FCSTD DOCUMENT  (FreeCAD 1.0R39109 (Git))
Label: barrel
License: All rights reserved
LicenseURL: https://en.wikipedia.org/wiki/All_rights_reserved
objects: App::Link×10, App::FeaturePython×9, Assembly::JointGroup×1, Assembly::AssemblyObject×1
EXTERNAL_REF file=barrelMount.FCStd obj=Body
EXTERNAL_REF file=barrelSpacer.FCStd obj=Body
EXTERNAL_REF file=barrelSideOpen.FCStd obj=Body
EXTERNAL_REF file=../roundFlap.FCStd obj=Body

FEATURE [App::Link] Body
  LinkedObject = -> <external barrelMount.FCStd>#Body
FEATURE [App::FeaturePython] GroundedJoint  # Assembly grounded joint (typed FeaturePython)
  ObjectToGround = -> Body
FEATURE [App::Link] Body001  label="Spacer1"
  LinkPlacement = pos=(58,31.8049,3.72e-14) rot=(0.57735,0.57735,-0.57735;4.18879rad)
  LinkedObject = -> <external barrelSpacer.FCStd>#Body
  Placement = pos=(58,31.8049,3.72e-14) rot=(0.57735,0.57735,-0.57735;4.18879rad)
FEATURE [App::Link] Body002  label="Spacer2"
  LinkPlacement = pos=(58,-1.99704,-31.7421) rot=(0.57735,0.57735,-0.57735;4.18879rad)
  LinkedObject = -> <external barrelSpacer.FCStd>#Body
  Placement = pos=(58,-1.99704,-31.7421) rot=(0.57735,0.57735,-0.57735;4.18879rad)
FEATURE [App::Link] Body003  label="Spacer3"
  LinkPlacement = pos=(3,-31.8049,1.15e-14) rot=(0.57735,0.57735,0.57735;2.0944rad)
  LinkedObject = -> <external barrelSpacer.FCStd>#Body
  Placement = pos=(3,-31.8049,1.15e-14) rot=(0.57735,0.57735,0.57735;2.0944rad)
FEATURE [App::Link] Body004  label="Spacer4"
  LinkPlacement = pos=(3,1.99704,31.7421) rot=(0.57735,0.57735,0.57735;2.0944rad)
  LinkedObject = -> <external barrelSpacer.FCStd>#Body
  Placement = pos=(3,1.99704,31.7421) rot=(0.57735,0.57735,0.57735;2.0944rad)
FEATURE [App::Link] Body007  label="SideOpen"
  LinkPlacement = pos=(61,3.75e-14,5.47e-14) rot=(0,1,0;3.14159rad)
  LinkedObject = -> <external barrelSideOpen.FCStd>#Body
  Placement = pos=(61,3.75e-14,5.47e-14) rot=(0,1,0;3.14159rad)
FEATURE [App::Link] Body008  label="Flap2"
  LinkPlacement = pos=(30.5,-35.345,41.8018) rot=(1,0,0;4.64956rad)
  LinkedObject = -> <external ../roundFlap.FCStd>#Body
  Placement = pos=(30.5,-35.345,41.8018) rot=(1,0,0;4.64956rad)
FEATURE [App::Link] Body009  label="Flap1"
  LinkPlacement = pos=(30.3278,-36.327,-41.8389) rot=(0,0.693562,0.720397;3.14159rad)
  LinkedObject = -> <external ../roundFlap.FCStd>#Body
  Placement = pos=(30.3278,-36.327,-41.8389) rot=(0,0.693562,0.720397;3.14159rad)
FEATURE [App::Link] Body010  label="Unnamed"
FEATURE [App::Link] Body011  label="Unnamed"
FEATURE [App::FeaturePython] Joint  label="Fixed"  # Assembly joint (typed FeaturePython)
  Activated = true
  AngleMax = 0
  AngleMin = 0
  Detach1 = false
  Detach2 = false
  Distance = 0
  Distance2 = 0
  EnableAngleMax = false
  EnableAngleMin = false
  EnableLengthMax = false
  EnableLengthMin = false
  JointType = 0 (Fixed)
  LengthMax = 0
  LengthMin = 0
  Placement2 = pos=(3,-31.8049,1.15e-14) rot=(0.57735,0.57735,0.57735;2.0944rad)
  Reference1 = -> Assembly [Body003.Pad.Edge5,Body003.Pad.Edge5]
  Reference2 = -> Assembly [Body.Chamfer001.Edge234,Body.Chamfer001.Edge234]
FEATURE [App::FeaturePython] Joint008  label="Fixed001"  # Assembly joint (typed FeaturePython)
  Activated = true
  AngleMax = 0
  AngleMin = 0
  Detach1 = false
  Detach2 = false
  Distance = 0
  Distance2 = 0
  EnableAngleMax = false
  EnableAngleMin = false
  EnableLengthMax = false
  EnableLengthMin = false
  JointType = 0 (Fixed)
  LengthMax = 0
  LengthMin = 0
  Placement1 = pos=(0,0,55) rot=(0,0,1;0rad)
  Placement2 = pos=(3,31.8049,-1.78e-14) rot=(0.57735,0.57735,0.57735;2.0944rad)
  Reference1 = -> Assembly [Body001.Pad.Edge6,Body001.Pad.Edge6]
  Reference2 = -> Assembly [Body.Chamfer001.Edge190,Body.Chamfer001.Edge190]
FEATURE [App::FeaturePython] Joint009  label="Fixed002"  # Assembly joint (typed FeaturePython)
  Activated = true
  AngleMax = 0
  AngleMin = 0
  Detach1 = false
  Detach2 = false
  Distance = 0
  Distance2 = 0
  EnableAngleMax = false
  EnableAngleMin = false
  EnableLengthMax = false
  EnableLengthMin = false
  JointType = 0 (Fixed)
  LengthMax = 0
  LengthMin = 0
  Placement2 = pos=(3,1.99704,31.7421) rot=(0.57735,0.57735,0.57735;2.0944rad)
  Reference1 = -> Assembly [Body004.Pad.Edge5,Body004.Pad.Edge5]
  Reference2 = -> Assembly [Body.Chamfer001.Edge184,Body.Chamfer001.Edge184]
FEATURE [App::FeaturePython] Joint010  label="Fixed003"  # Assembly joint (typed FeaturePython)
  Activated = true
  AngleMax = 0
  AngleMin = 0
  Detach1 = false
  Detach2 = false
  Distance = 0
  Distance2 = 0
  EnableAngleMax = false
  EnableAngleMin = false
  EnableLengthMax = false
  EnableLengthMin = false
  JointType = 0 (Fixed)
  LengthMax = 0
  LengthMin = 0
  Placement1 = pos=(0,0,55) rot=(0,0,1;0rad)
  Placement2 = pos=(3,-1.99704,-31.7421) rot=(0.57735,0.57735,0.57735;2.0944rad)
  Reference1 = -> Assembly [Body002.Pad.Edge6,Body002.Pad.Edge6]
  Reference2 = -> Assembly [Body.Chamfer001.Edge240,Body.Chamfer001.Edge240]
FEATURE [App::FeaturePython] Joint011  label="Fixed004"  # Assembly joint (typed FeaturePython)
  Activated = true
  AngleMax = 0
  AngleMin = 0
  Detach1 = false
  Detach2 = false
  Distance = 0
  Distance2 = 0
  EnableAngleMax = false
  EnableAngleMin = false
  EnableLengthMax = false
  EnableLengthMin = false
  JointType = 0 (Fixed)
  LengthMax = 0
  LengthMin = 0
  Placement1 = pos=(3,-31.8049,6e-16) rot=(0.57735,0.57735,0.57735;2.0944rad)
  Placement2 = pos=(0,0,55) rot=(0,0,1;0rad)
  Reference1 = -> Assembly [Body007.Pocket001.Edge107,Body007.Pocket001.Edge107]
  Reference2 = -> Assembly [Body003.Pad.Edge6,Body003.Pad.Edge6]
FEATURE [App::FeaturePython] Joint012  label="Fixed005"  # Assembly joint (typed FeaturePython)
  Activated = true
  AngleMax = 0
  AngleMin = 0
  Detach1 = false
  Detach2 = false
  Distance = 0
  Distance2 = 0
  EnableAngleMax = false
  EnableAngleMin = false
  EnableLengthMax = false
  EnableLengthMin = false
  JointType = 0 (Fixed)
  LengthMax = 0
  LengthMin = 0
  Placement1 = pos=(3,31.8049,-2e-16) rot=(0.57735,0.57735,0.57735;2.0944rad)
  Reference1 = -> Assembly [Body007.Pocket001.Edge75,Body007.Pocket001.Edge75]
  Reference2 = -> Assembly [Body001.Pad.Edge5,Body001.Pad.Edge5]
FEATURE [App::FeaturePython] Joint013  label="Cylindrical"  # Assembly joint (typed FeaturePython)
  Activated = true
  AngleMax = 0
  AngleMin = 0
  Detach1 = false
  Detach2 = false
  Distance = 0
  Distance2 = 0
  EnableAngleMax = false
  EnableAngleMin = false
  EnableLengthMax = false
  EnableLengthMin = false
  JointType = 2 (Cylindrical)
  LengthMax = 0
  LengthMin = 0
  Placement1 = pos=(29,39.5,0.5) rot=(0.576441,-0.576441,-0.576441;2.0944rad)
  Placement2 = pos=(1.5,-37.3262,-2.34837) rot=(0.706932,-0.022216,0.706932;3.18602rad)
  Reference1 = -> Assembly [Body009.Face8,Body009.Face8]
  Reference2 = -> Assembly [Body.Face66,Body.Face66]
FEATURE [App::FeaturePython] Joint014  label="Cylindrical001"  # Assembly joint (typed FeaturePython)
  Activated = true
  AngleMax = 0
  AngleMin = 0
  Detach1 = false
  Detach2 = false
  Distance = 0
  Distance2 = 0
  EnableAngleMax = false
  EnableAngleMin = false
  EnableLengthMax = false
  EnableLengthMin = false
  JointType = 2 (Cylindrical)
  LengthMax = 0
  LengthMin = 0
  Placement1 = pos=(-29,39.5,0.5) rot=(-0.57735,0.57735,0.57735;4.18879rad)
  Placement2 = pos=(1.5,-37.3262,2.34837) rot=(0.706932,0.022216,0.706932;3.09717rad)
  Reference1 = -> Assembly [Body008.Face2,Body008.Face2]
  Reference2 = -> Assembly [Body.Face60,Body.Face60]
FEATURE [Assembly::JointGroup] Joints
  Group = -> [GroundedJoint,Joint,Joint008,Joint009,Joint010,Joint011,Joint012,Joint013,Joint014]
FEATURE [Assembly::AssemblyObject] Assembly
  Group = -> [Joints,Body,GroundedJoint,Body001,Body002,Body003,Body004,Body007,Body008,Body009,Joint,Joint008,Joint009,Joint010,Joint011,Joint012,Joint013,Joint014]
  Origin = -> Origin
  Type = Assembly

RESOLVED EXTERNAL PARTS (link-assembly join: the EXTERNAL_REF files above that resolve inside this repo's crawl, each included once):
---- part ../roundFlap.FCStd = doc fcstd_2553a03e6fe1 ----
FCSTD DOCUMENT  (FreeCAD 1.0R39109 (Git))
Label: roundFlap
License: All rights reserved
LicenseURL: https://en.wikipedia.org/wiki/All_rights_reserved
objects: Sketcher::SketchObject×2, PartDesign::Pad×2, PartDesign::Mirrored×1, PartDesign::Body×1
note: 13 computed .brp shape members not serialized (recipe doc carries the construction recipe); baked Part::Feature solids carry a one-line shape summary decoded from their .brp

FEATURE [Sketcher::SketchObject] Sketch
  ArcFitTolerance = 1e-06
  AttachmentSupport = -> [XY_Plane]
  FullyConstrained = true
  MakeInternals = false
  MapMode = 5
  sketch-geometry (5):
    g0: LineSegment StartX=-27 StartY=0 StartZ=0 EndX=0 EndY=0 EndZ=0
    g1: LineSegment StartX=0 StartY=0 StartZ=0 EndX=0 EndY=40 EndZ=0
    g2: LineSegment StartX=0 StartY=40 StartZ=0 EndX=-27 EndY=40 EndZ=0
    g3: LineSegment StartX=-27 StartY=40 StartZ=0 EndX=-27 EndY=0 EndZ=0
    g4: GeomPoint [constr] X=0 Y=0 Z=0
  constraints (12):
    c: Coincident(g0,g1)
    c: Coincident(g1,g2)
    c: Coincident(g2,g3)
    c: Coincident(g3,g0)
    c: Horizontal(g0)
    c: Horizontal(g2)
    c: Vertical(g1)
    c: Vertical(g3)
    c: Coincident(g4,g-1)
    c: Distance(g0,g2) = 40
    c: Coincident(g0,g4)
    c: DistanceX(g0,g0) = 27
FEATURE [PartDesign::Pad] Pad
  Direction = (0,0,1)
  Length = 1
  Length2 = 10
  Profile = -> Sketch
  ReferenceAxis = -> Sketch [N_Axis]
  Refine = true
  Suppressed = false
  Type = 0
FEATURE [Sketcher::SketchObject] Sketch001
  ArcFitTolerance = 1e-06
  AttachmentSupport = -> [Pad]
  FullyConstrained = true
  MakeInternals = false
  MapMode = 5
  Placement = pos=(-27,0,0) rot=(0.57735,-0.57735,-0.57735;2.0944rad)
  sketch-geometry (1):
    g0: Circle CenterX=-39.5 CenterY=0.5 CenterZ=0 NormalX=0 NormalY=0 NormalZ=1 AngleXU=0 Radius=0.5
  constraints (3):
    c: Tangent(g0,g-1)
    c: Diameter(g0) = 1
    c: DistanceX(g0,g-1) = 39.5
FEATURE [PartDesign::Pad] Pad001
  BaseFeature = -> Pad
  Direction = (-1,0,0)
  Length = 4
  Length2 = 10
  Profile = -> Sketch001
  ReferenceAxis = -> Sketch001 [N_Axis]
  Refine = true
  Suppressed = false
  Type = 0
FEATURE [PartDesign::Mirrored] Mirrored
  BaseFeature = -> Pad001
  MirrorPlane = -> YZ_Plane
  Refine = true
  Suppressed = false
  TransformMode = 1
FEATURE [PartDesign::Body] Body
  AllowCompound = false
  Group = -> [Sketch,Pad,Sketch001,Pad001,Mirrored]
  Origin = -> Origin
  Tip = -> Mirrored
---- part barrelMount.FCStd = doc fcstd_386b91f5edca ----
FCSTD DOCUMENT  (FreeCAD 1.0R39109 (Git))
Label: barrelMount
License: All rights reserved
LicenseURL: https://en.wikipedia.org/wiki/All_rights_reserved
objects: Sketcher::SketchObject×5, PartDesign::Pocket×3, PartDesign::Pad×2, PartDesign::Fillet×2, PartDesign::Chamfer×2, PartDesign::PolarPattern×1, PartDesign::Body×1
note: 40 computed .brp shape members not serialized (recipe doc carries the construction recipe); baked Part::Feature solids carry a one-line shape summary decoded from their .brp

FEATURE [Sketcher::SketchObject] Sketch
  ArcFitTolerance = 1e-06
  AttachmentSupport = -> [YZ_Plane]
  FullyConstrained = false
  MakeInternals = false
  MapMode = 5
  Placement = pos=(0,0,0) rot=(0.57735,0.57735,0.57735;2.0944rad)
  sketch-geometry (2):
    g0: Circle CenterX=0 CenterY=0 CenterZ=0 NormalX=0 NormalY=0 NormalZ=1 AngleXU=0 Radius=40
    g1: GeomPoint [constr] X=0 Y=0 Z=0
  constraints (1):
    c: Diameter(g0) = 80
FEATURE [PartDesign::Pad] Pad
  Direction = (1,0,0)
  Length = 3
  Length2 = 10
  Placement = pos=(0,0,0) rot=(1,1,1;2.0944rad)
  Profile = -> Sketch
  ReferenceAxis = -> Sketch [N_Axis]
  Refine = true
  Suppressed = false
  Type = 0
FEATURE [Sketcher::SketchObject] Sketch001
  ArcFitTolerance = 1e-06
  AttachmentSupport = -> [Pad]
  ExternalGeometry = -> [Pad]
  FullyConstrained = true
  MakeInternals = false
  MapMode = 5
  Placement = pos=(3,0,0) rot=(0.57735,0.57735,0.57735;2.0944rad)
  sketch-geometry (1):
    g0: Circle CenterX=0 CenterY=37.4 CenterZ=0 NormalX=0 NormalY=0 NormalZ=1 AngleXU=0 Radius=1.6
  constraints (3):
    c: PointOnObject(g0,g-2)
    c: Diameter(g0) = 3.2
    c: Distance(g0,g-3) = 1
FEATURE [PartDesign::Pocket] Pocket
  BaseFeature = -> Pad
  Direction = (-1,0,0)
  Length = 5
  Length2 = 5
  Placement = pos=(0,0,0) rot=(1,1,1;2.0944rad)
  Profile = -> Sketch001
  ReferenceAxis = -> Sketch001 [N_Axis]
  Refine = true
  Suppressed = false
  Type = 1
FEATURE [PartDesign::PolarPattern] PolarPattern
  Angle = 360
  Axis = -> Sketch001 [N_Axis]
  BaseFeature = -> Pocket
  Mode = 0
  Occurrences = 50
  Offset = 120
  Originals = -> [Pocket]
  Placement = pos=(0,0,0) rot=(1,1,1;2.0944rad)
  Refine = true
  Suppressed = false
  TransformMode = 0
FEATURE [Sketcher::SketchObject] Sketch002
  ArcFitTolerance = 1e-06
  AttachmentSupport = -> [PolarPattern]
  ExternalGeometry = -> [PolarPattern]
  FullyConstrained = true
  MakeInternals = false
  MapMode = 5
  Placement = pos=(3,0,0) rot=(0.57735,0.57735,0.57735;2.0944rad)
  sketch-geometry (27):
    g0: Circle [constr] CenterX=0 CenterY=0 CenterZ=0 NormalX=0 NormalY=0 NormalZ=1 AngleXU=0 Radius=31.5
    g1: Circle CenterX=1.99704 CenterY=31.7421 CenterZ=0 NormalX=0 NormalY=0 NormalZ=1 AngleXU=0 Radius=1.6
    g2: Circle CenterX=31.8049 CenterY=1.18e-14 CenterZ=0 NormalX=0 NormalY=0 NormalZ=1 AngleXU=0 Radius=1.6
    g3: Circle CenterX=-1.99704 CenterY=-31.7421 CenterZ=0 NormalX=0 NormalY=0 NormalZ=1 AngleXU=0 Radius=1.6
    g4: Circle CenterX=-31.8049 CenterY=-8.4e-15 CenterZ=0 NormalX=0 NormalY=0 NormalZ=1 AngleXU=0 Radius=1.6
    g5: ArcOfCircle CenterX=1.99704 CenterY=31.7421 CenterZ=0 NormalX=0 NormalY=0 NormalZ=1 AngleXU=0 Radius=4.6 StartAngle=4.82195 EndAngle=6.08164
    g6: LineSegment StartX=-2.5 StartY=31.4006 StartZ=0 EndX=-2.5 EndY=2.5 EndZ=0
    g7: LineSegment StartX=2.5 StartY=2.5 StartZ=0 EndX=2.5 EndY=27.1697 EndZ=0
    g8: LineSegment StartX=2.5 StartY=-2.5 StartZ=0 EndX=2.5 EndY=-31.4006 EndZ=0
    g9: LineSegment StartX=-2.5 StartY=-27.1697 StartZ=0 EndX=-2.5 EndY=-2.5 EndZ=0
    g10: ArcOfCircle CenterX=0 CenterY=0 CenterZ=0 NormalX=0 NormalY=0 NormalZ=1 AngleXU=0 Radius=31.5 StartAngle=0.145138 EndAngle=1.36283
    g11: ArcOfCircle CenterX=0 CenterY=0 CenterZ=0 NormalX=0 NormalY=0 NormalZ=1 AngleXU=0 Radius=31.5 StartAngle=4.79184 EndAngle=6.13805
    g12: ArcOfCircle CenterX=0 CenterY=0 CenterZ=0 NormalX=0 NormalY=0 NormalZ=1 AngleXU=0 Radius=31.5 StartAngle=1.65024 EndAngle=2.99645
    g13: ArcOfCircle CenterX=0 CenterY=0 CenterZ=0 NormalX=0 NormalY=0 NormalZ=1 AngleXU=0 Radius=31.5 StartAngle=3.28673 EndAngle=4.50442
    g14: ArcOfCircle CenterX=31.8049 CenterY=1.18e-14 CenterZ=0 NormalX=0 NormalY=0 NormalZ=1 AngleXU=0 Radius=4.6 StartAngle=3.71617 EndAngle=4.57367
    g15: Circle [constr] CenterX=-1.99704 CenterY=-31.7421 CenterZ=0 NormalX=0 NormalY=0 NormalZ=1 AngleXU=0 Radius=4.6
    g16: Circle [constr] CenterX=31.8049 CenterY=1.18e-14 CenterZ=0 NormalX=0 NormalY=0 NormalZ=1 AngleXU=0 Radius=4.6
    g17: Circle [constr] CenterX=1.99704 CenterY=31.7421 CenterZ=0 NormalX=0 NormalY=0 NormalZ=1 AngleXU=0 Radius=4.6
    g18: Circle [constr] CenterX=-31.8049 CenterY=-8.4e-15 CenterZ=0 NormalX=0 NormalY=0 NormalZ=1 AngleXU=0 Radius=4.6
    g19: ArcOfCircle CenterX=-1.99704 CenterY=-31.7421 CenterZ=0 NormalX=0 NormalY=0 NormalZ=1 AngleXU=0 Radius=4.6 StartAngle=1.68035 EndAngle=2.94004
    g20: ArcOfCircle CenterX=-31.8049 CenterY=-8.4e-15 CenterZ=0 NormalX=0 NormalY=0 NormalZ=1 AngleXU=0 Radius=4.6 StartAngle=0.574575 EndAngle=1.43208
    g21: ArcOfCircle CenterX=-31.8049 CenterY=-8.4e-15 CenterZ=0 NormalX=0 NormalY=0 NormalZ=1 AngleXU=0 Radius=4.6 StartAngle=4.85111 EndAngle=5.70861
    g22: LineSegment StartX=-2.5 StartY=2.5 StartZ=0 EndX=-27.9435 EndY=2.5 EndZ=0
    g23: LineSegment StartX=-2.5 StartY=-2.5 StartZ=0 EndX=-27.9435 EndY=-2.5 EndZ=0
    g24: LineSegment StartX=2.5 StartY=-2.5 StartZ=0 EndX=27.9435 EndY=-2.5 EndZ=0
    g25: LineSegment StartX=2.5 StartY=2.5 StartZ=0 EndX=27.9435 EndY=2.5 EndZ=0
    g26: ArcOfCircle CenterX=31.8049 CenterY=1.18e-14 CenterZ=0 NormalX=0 NormalY=0 NormalZ=1 AngleXU=0 Radius=4.6 StartAngle=1.70951 EndAngle=2.56702
  constraints (76):
    c: Coincident(g0,g-1)
    c: Coincident(g5,g1)
    c: Distance(g2,g-6) = 6
    c: Distance(g-5,g2) = 6
    c: Distance(g1,g-3) = 6
    c: Distance(g1,g-4) = 6
    c: Distance(g-7,g4) = 6
    c: Distance(g-8,g4) = 6
    c: Diameter(g1) = 3.2
    c: Equal(g1,g2)
    c: Equal(g2,g3)
    c: Equal(g3,g4)
    c: Vertical(g6)
    c: Vertical(g7)
    c: Vertical(g8)
    c: Vertical(g9)
    c: Coincident(g7,g5)
    c: Coincident(g10,g0)
    c: Coincident(g10,g5)
    c: Coincident(g11,g0)
    c: Coincident(g11,g8)
    c: Coincident(g12,g0)
    c: Coincident(g12,g6)
    c: PointOnObject(g5,g0)
    c: PointOnObject(g13,g0)
    c: Distance(g7,g6) = 5
    c: Distance(g6,g-2) = 2.5
    c: Distance(g7,g-1) = 2.5
    c: PointOnObject(g6,g0)
    c: PointOnObject(g8,g0)
    c: Coincident(g13,g0)
    c: Distance(g6,g-1) = 2.5
    c: Distance(g9,g8) = 5
    c: Distance(g9,g-2) = 2.5
    c: Coincident(g14,g2)
    c: Coincident(g15,g3)
    c: Coincident(g16,g2)
    c: Coincident(g17,g1)
    c: Coincident(g18,g4)
    c: Distance(g18,g4) = 3
    c: Distance(g2,g16) = 3
    c: Coincident(g11,g14)
    c: PointOnObject(g11,g16)
    c: Coincident(g19,g3)
    c: Coincident(g19,g9)
    c: Coincident(g19,g13)
    c: Coincident(g20,g4)
    c: PointOnObject(g20,g18)
    c: Coincident(g21,g4)
    c: PointOnObject(g21,g18)
    c: Coincident(g13,g21)
    c: Coincident(g20,g12)
    c: Coincident(g22,g6)
    c: Horizontal(g22)
    c: Coincident(g24,g8)
    c: Horizontal(g24)
    c: Coincident(g25,g7)
    c: Horizontal(g25)
    c: Coincident(g26,g2)
    c: PointOnObject(g26,g16)
    c: Coincident(g26,g10)
    c: Coincident(g25,g26)
    c: Coincident(g14,g24)
    c: Coincident(g9,g23)
    c: Horizontal(g23)
    c: Coincident(g23,g21)
    c: Coincident(g22,g20)
    c: PointOnObject(g13,g15)
    c: Distance(g3,g15) = 3
    c: Distance(g22,g23) = 5
    c: Distance(g24,g25) = 5
    c: Distance(g10,g-9) = 8.5
    c: Distance(g3,g-11) = 6
    c: Distance(g-10,g3) = 6
    c: Distance(g1,g17) = 3
    c: PointOnObject(g5,g17)
FEATURE [PartDesign::Pocket] Pocket001
  BaseFeature = -> PolarPattern
  Direction = (-1,0,0)
  Length = 5
  Length2 = 5
  Placement = pos=(0,0,0) rot=(1,1,1;2.0944rad)
  Profile = -> Sketch002
  ReferenceAxis = -> Sketch002 [N_Axis]
  Refine = true
  Suppressed = false
  Type = 1
FEATURE [Sketcher::SketchObject] Sketch003
  ArcFitTolerance = 1e-06
  AttachmentSupport = -> [YZ_Plane]
  FullyConstrained = true
  MakeInternals = false
  MapMode = 5
  Placement = pos=(0,0,0) rot=(0.57735,0.57735,0.57735;2.0944rad)
  sketch-geometry (1):
    g0: Circle CenterX=0 CenterY=0 CenterZ=0 NormalX=0 NormalY=0 NormalZ=1 AngleXU=0 Radius=10
  constraints (2):
    c: Coincident(g0,g-1)
    c: Diameter(g0) = 20
FEATURE [PartDesign::Pad] Pad001
  BaseFeature = -> Pocket001
  Direction = (1,0,0)
  Length = 15
  Length2 = 10
  Placement = pos=(0,0,0) rot=(1,1,1;2.0944rad)
  Profile = -> Sketch003
  ReferenceAxis = -> Sketch003 [N_Axis]
  Refine = true
  Suppressed = false
  Type = 0
FEATURE [Sketcher::SketchObject] Sketch004
  ArcFitTolerance = 1e-06
  AttachmentSupport = -> [Pad001]
  FullyConstrained = true
  MakeInternals = false
  MapMode = 5
  Placement = pos=(15,0,0) rot=(0.57735,0.57735,0.57735;2.0944rad)
  sketch-geometry (5):
    g0: LineSegment [constr] StartX=-1.5 StartY=2 StartZ=0 EndX=1.5 EndY=2 EndZ=0
    g1: ArcOfCircle [constr] CenterX=0 CenterY=0 CenterZ=0 NormalX=0 NormalY=0 NormalZ=1 AngleXU=0 Radius=2.5 StartAngle=2.2143 EndAngle=7.21048
    g2: Circle [constr] CenterX=0 CenterY=0 CenterZ=0 NormalX=0 NormalY=0 NormalZ=1 AngleXU=0 Radius=2.5
    g3: ArcOfCircle CenterX=0 CenterY=0 CenterZ=0 NormalX=0 NormalY=0 NormalZ=1 AngleXU=0 Radius=2.65 StartAngle=2.19518 EndAngle=7.22959
    g4: LineSegment StartX=-1.54919 StartY=2.15 StartZ=0 EndX=1.54919 EndY=2.15 EndZ=0
  constraints (14):
    c: Horizontal(g0)
    c: Coincident(g1,g-1)
    c: Coincident(g1,g0)
    c: Coincident(g1,g0)
    c: Coincident(g2,g1)
    c: PointOnObject(g0,g2)
    c: Diameter(g2) = 5
    c: Distance(g2,g0) = -0.5
    c: Coincident(g3,g1)
    c: Coincident(g4,g3)
    c: Coincident(g4,g3)
    c: Horizontal(g4)
    c: Distance(g1,g3) = 0.15
    c: Distance(g0,g4) = 0.15
FEATURE [PartDesign::Pocket] Pocket002
  BaseFeature = -> Pad001
  Direction = (-1,0,0)
  Length = 5
  Length2 = 5
  Placement = pos=(0,0,0) rot=(1,1,1;2.0944rad)
  Profile = -> Sketch004
  ReferenceAxis = -> Sketch004 [N_Axis]
  Refine = true
  Suppressed = false
  Type = 1
FEATURE [PartDesign::Fillet] Fillet
  Base = -> Pocket002 [Edge186,Edge208,Edge184,Edge173,Edge198,Edge197,Edge226,Edge227,Edge224,Edge225,Edge210,Edge209,Edge196,Edge185]
  BaseFeature = -> Pocket002
  Placement = pos=(0,0,0) rot=(1,1,1;2.0944rad)
  Radius = 3
  Refine = true
  SupportTransform = false
  Suppressed = false
  UseAllEdges = false
FEATURE [PartDesign::Chamfer] Chamfer
  Angle = 45
  Base = -> Fillet [Edge104,Edge107,Edge110,Edge99,Edge101]
  BaseFeature = -> Fillet
  ChamferType = 1
  FlipDirection = false
  Placement = pos=(0,0,0) rot=(1,1,1;2.0944rad)
  Refine = true
  Size = 11.99
  Size2 = 15
  SupportTransform = false
  Suppressed = false
  UseAllEdges = false
FEATURE [PartDesign::Fillet] Fillet001
  Base = -> Chamfer [Edge109,Edge108,Edge106,Edge105,Edge6,Edge4,Edge114,Edge112,Edge124,Edge125,Edge120,Edge118,Edge119,Edge121,Edge115,Edge113]
  BaseFeature = -> Chamfer
  Placement = pos=(0,0,0) rot=(1,1,1;2.0944rad)
  Radius = 3
  Refine = true
  SupportTransform = false
  Suppressed = false
  UseAllEdges = false
FEATURE [PartDesign::Chamfer] Chamfer001
  Angle = 45
  Base = -> Fillet001 [Edge328,Edge325]
  BaseFeature = -> Fillet001
  ChamferType = 0
  FlipDirection = false
  Placement = pos=(0,0,0) rot=(1,1,1;2.0944rad)
  Refine = true
  Size = 1.5
  Size2 = 1
  SupportTransform = false
  Suppressed = false
  UseAllEdges = false
FEATURE [PartDesign::Body] Body
  AllowCompound = false
  Group = -> [Sketch,Pad,Sketch001,Pocket,PolarPattern,Sketch002,Pocket001,Sketch003,Pad001,Sketch004,Pocket002,Fillet,Chamfer,Fillet001,Chamfer001]
  Origin = -> Origin
  Tip = -> Chamfer001
---- part barrelSideOpen.FCStd = doc fcstd_5df076a25a03 ----
FCSTD DOCUMENT  (FreeCAD 1.0R39109 (Git))
Label: barrelSideOpen
License: All rights reserved
LicenseURL: https://en.wikipedia.org/wiki/All_rights_reserved
objects: Sketcher::SketchObject×3, PartDesign::Pocket×2, PartDesign::Pad×1, PartDesign::PolarPattern×1, PartDesign::Body×1
note: 18 computed .brp shape members not serialized (recipe doc carries the construction recipe); baked Part::Feature solids carry a one-line shape summary decoded from their .brp

FEATURE [Sketcher::SketchObject] Sketch
  ArcFitTolerance = 1e-06
  AttachmentSupport = -> [YZ_Plane]
  FullyConstrained = true
  MakeInternals = false
  MapMode = 5
  Placement = pos=(0,0,0) rot=(0.57735,0.57735,0.57735;2.0944rad)
  sketch-geometry (2):
    g0: Circle CenterX=0 CenterY=0 CenterZ=0 NormalX=0 NormalY=0 NormalZ=1 AngleXU=0 Radius=28
    g1: Circle CenterX=0 CenterY=0 CenterZ=0 NormalX=0 NormalY=0 NormalZ=1 AngleXU=0 Radius=40
  constraints (4):
    c: Coincident(g1,g0)
    c: Distance(g1,g0) = 12
    c: Diameter(g1) = 80
    c: Coincident(g0,g-1)
FEATURE [PartDesign::Pad] Pad
  Direction = (1,0,0)
  Length = 3
  Length2 = 10
  Placement = pos=(0,0,0) rot=(1,1,1;2.0944rad)
  Profile = -> Sketch
  ReferenceAxis = -> Sketch [N_Axis]
  Refine = true
  Suppressed = false
  Type = 0
FEATURE [Sketcher::SketchObject] Sketch001
  ArcFitTolerance = 1e-06
  AttachmentSupport = -> [Pad]
  ExternalGeometry = -> [Pad]
  FullyConstrained = true
  MakeInternals = false
  MapMode = 5
  Placement = pos=(3,0,0) rot=(0.57735,0.57735,0.57735;2.0944rad)
  sketch-geometry (1):
    g0: Circle CenterX=0 CenterY=37.4 CenterZ=0 NormalX=0 NormalY=0 NormalZ=1 AngleXU=0 Radius=1.6
  constraints (3):
    c: PointOnObject(g0,g-2)
    c: Diameter(g0) = 3.2
    c: Distance(g-3,g0) = 1
FEATURE [PartDesign::Pocket] Pocket
  BaseFeature = -> Pad
  Direction = (-1,0,0)
  Length = 5
  Length2 = 5
  Placement = pos=(0,0,0) rot=(1,1,1;2.0944rad)
  Profile = -> Sketch001
  ReferenceAxis = -> Sketch001 [N_Axis]
  Refine = true
  Suppressed = false
  Type = 0
FEATURE [PartDesign::PolarPattern] PolarPattern
  Angle = 360
  Axis = -> Sketch001 [N_Axis]
  BaseFeature = -> Pocket
  Mode = 0
  Occurrences = 50
  Offset = 120
  Originals = -> [Pocket]
  Placement = pos=(0,0,0) rot=(1,1,1;2.0944rad)
  Refine = true
  Suppressed = false
  TransformMode = 0
FEATURE [Sketcher::SketchObject] Sketch002
  ArcFitTolerance = 1e-06
  AttachmentSupport = -> [PolarPattern]
  ExternalGeometry = -> [PolarPattern]
  FullyConstrained = true
  MakeInternals = false
  MapMode = 5
  Placement = pos=(3,0,0) rot=(0.57735,0.57735,0.57735;2.0944rad)
  sketch-geometry (5):
    g0: Circle CenterX=1.99704 CenterY=31.7421 CenterZ=0 NormalX=0 NormalY=0 NormalZ=1 AngleXU=0 Radius=1.6
    g1: Circle CenterX=31.8049 CenterY=1.19e-14 CenterZ=0 NormalX=0 NormalY=0 NormalZ=1 AngleXU=0 Radius=1.6
    g2: Circle CenterX=-31.8049 CenterY=-8.4e-15 CenterZ=0 NormalX=0 NormalY=0 NormalZ=1 AngleXU=0 Radius=1.6
    g3: Circle CenterX=-1.99704 CenterY=-31.7421 CenterZ=0 NormalX=0 NormalY=0 NormalZ=1 AngleXU=0 Radius=1.6
    g4: Circle CenterX=22.8172 CenterY=21.9489 CenterZ=0 NormalX=0 NormalY=0 NormalZ=1 AngleXU=0 Radius=2.5
  constraints (15):
    c: Distance(g-10,g3) = 6
    c: Distance(g3,g-9) = 6
    c: Distance(g1,g-8) = 6
    c: Distance(g-7,g1) = 6
    c: Distance(g-5,g0) = 6
    c: Distance(g0,g-6) = 6
    c: Distance(g-4,g2) = 6
    c: Distance(g2,g-3) = 6
    c: Diameter(g2) = 3.2
    c: Diameter(g1) = 3.2
    c: Diameter(g0) = 3.2
    c: Diameter(g3) = 3.2
    c: Diameter(g4) = 5
    c: Distance(g-11,g4) = 6
    c: DistanceX(g4,g-12) = 6
FEATURE [PartDesign::Pocket] Pocket001
  BaseFeature = -> PolarPattern
  Direction = (-1,0,0)
  Length = 5
  Length2 = 5
  Placement = pos=(0,0,0) rot=(1,1,1;2.0944rad)
  Profile = -> Sketch002
  ReferenceAxis = -> Sketch002 [N_Axis]
  Refine = true
  Suppressed = false
  Type = 1
FEATURE [PartDesign::Body] Body
  AllowCompound = false
  Group = -> [Sketch,Pad,Sketch001,Pocket,PolarPattern,Sketch002,Pocket001]
  Origin = -> Origin
  Tip = -> Pocket001
---- part barrelSpacer.FCStd = doc fcstd_c1fa6ff1a89d ----
FCSTD DOCUMENT  (FreeCAD 1.0R39109 (Git))
Label: barrelSpacer
License: All rights reserved
LicenseURL: https://en.wikipedia.org/wiki/All_rights_reserved
objects: Sketcher::SketchObject×1, PartDesign::Pad×1, PartDesign::Body×1
note: 6 computed .brp shape members not serialized (recipe doc carries the construction recipe); baked Part::Feature solids carry a one-line shape summary decoded from their .brp

FEATURE [Sketcher::SketchObject] Sketch
  ArcFitTolerance = 1e-06
  AttachmentSupport = -> [XY_Plane]
  FullyConstrained = true
  MakeInternals = false
  MapMode = 5
  sketch-geometry (2):
    g0: Circle CenterX=0 CenterY=0 CenterZ=0 NormalX=0 NormalY=0 NormalZ=1 AngleXU=0 Radius=1.5
    g1: Circle CenterX=0 CenterY=0 CenterZ=0 NormalX=0 NormalY=0 NormalZ=1 AngleXU=0 Radius=4
  constraints (4):
    c: Coincident(g0,g-1)
    c: Coincident(g1,g0)
    c: Diameter(g0) = 3
    c: Distance(g0,g1) = 2.5
FEATURE [PartDesign::Pad] Pad
  Direction = (0,0,1)
  Length = 55
  Length2 = 10
  Profile = -> Sketch
  ReferenceAxis = -> Sketch [N_Axis]
  Refine = true
  Suppressed = false
  Type = 0
FEATURE [PartDesign::Body] Body
  AllowCompound = false
  Group = -> [Sketch,Pad]
  Origin = -> Origin
  Tip = -> Pad
